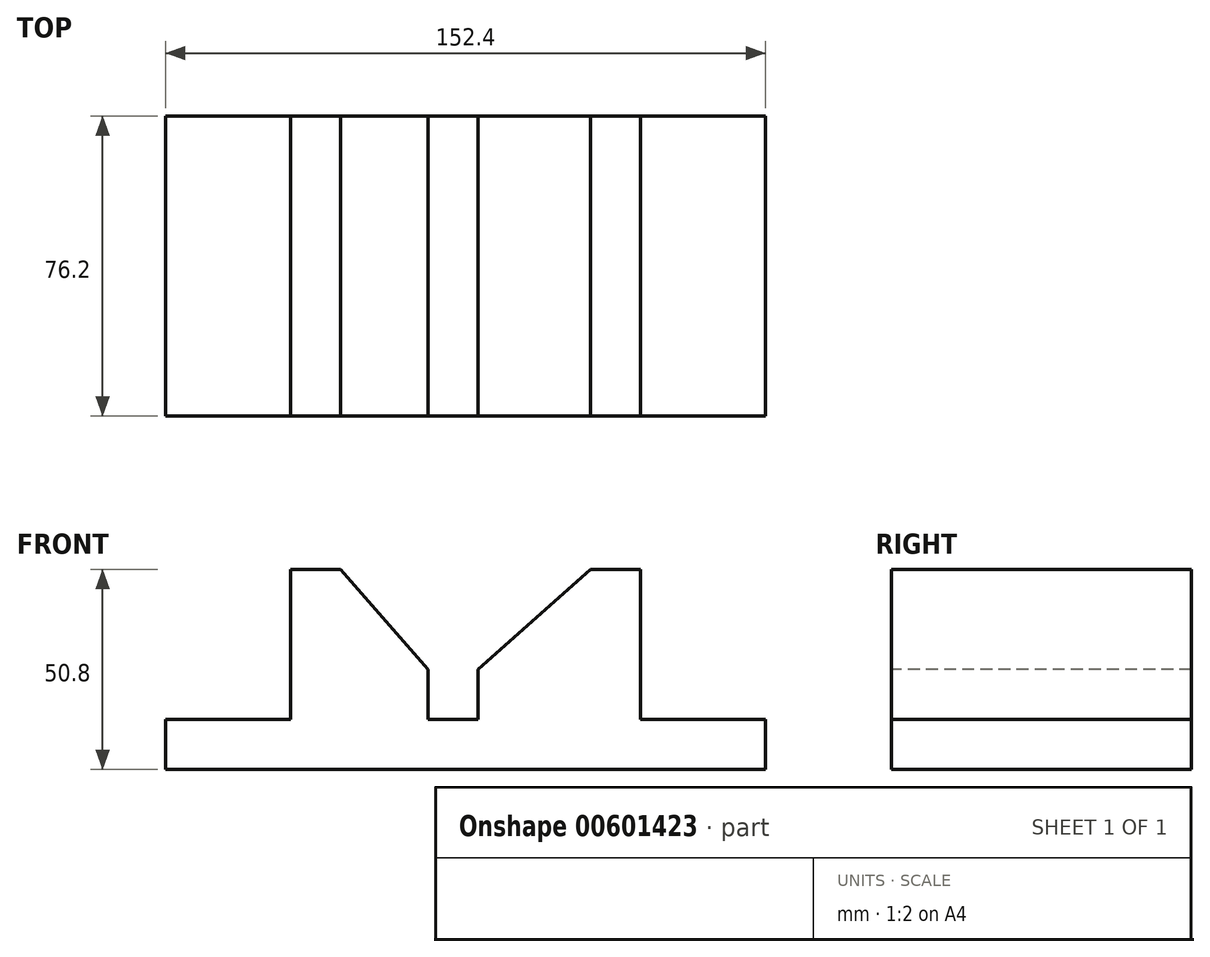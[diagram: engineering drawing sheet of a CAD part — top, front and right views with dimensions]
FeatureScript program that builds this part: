
annotation { "Feature Type Name" : "Feature", "Feature Type Description" : "" }
export const myFeature = defineFeature(function(context is Context, id is Id, definition is map)
    precondition{}
    {
        {
            var Q0;
            Q0=qCreatedBy(makeId("Front.planeOp"),FACE);
            var sketch = newSketch(context, id + "F0", { "sketchPlane" : qUnion([Q0])});
            skLineSegment(sketch, "E0", {"start": v(0, 0) * mm, "end": v(0, 12.7) * mm});
            skLineSegment(sketch, "E1", {"start": v(0, 12.7) * mm, "end": v(31.75, 12.7) * mm});
            skLineSegment(sketch, "E2", {"start": v(31.75, 12.7) * mm, "end": v(31.75, 50.8) * mm});
            skLineSegment(sketch, "E3", {"start": v(31.75, 50.8) * mm, "end": v(44.45, 50.8) * mm});
            skLineSegment(sketch, "E4", {"start": v(44.45, 50.8) * mm, "end": v(66.63, 25.4) * mm});
            skLineSegment(sketch, "E5", {"start": v(66.63, 25.4) * mm, "end": v(66.63, 12.7) * mm});
            skLineSegment(sketch, "E6", {"start": v(66.63, 12.7) * mm, "end": v(79.33, 12.7) * mm});
            skLineSegment(sketch, "E7", {"start": v(79.33, 12.7) * mm, "end": v(79.33, 25.4) * mm});
            skLineSegment(sketch, "E8", {"start": v(79.33, 25.4) * mm, "end": v(107.95, 50.8) * mm});
            skLineSegment(sketch, "E9", {"start": v(107.95, 50.8) * mm, "end": v(120.65, 50.8) * mm});
            skLineSegment(sketch, "E10", {"start": v(120.65, 50.8) * mm, "end": v(120.65, 12.7) * mm});
            skLineSegment(sketch, "E11", {"start": v(120.65, 12.7) * mm, "end": v(152.4, 12.7) * mm});
            skLineSegment(sketch, "E12", {"start": v(152.4, 12.7) * mm, "end": v(152.4, 0) * mm});
            skLineSegment(sketch, "E13", {"start": v(152.4, 0) * mm, "end": v(0, 0) * mm});
            skSolve(sketch);
        }
        {
            var Q0;
            Q0=makeQuery(id+"F0.imprint","IMPRINT",FACE,{"disambiguationData":[TD([[makeQuery(id+"F0.imprint","IMPRINT",EDGE,{"derivedFrom":sQuery(id+"F0.wireOp",EDGE,"E0")}),-1.0]])]});
            extrude(context, id + "F1", {"entities" : qUnion([Q0]), "oppositeDirection" : true, "depth" : 76.2 * mm, "offsetDistance" : 25.4 * mm});
        }
    });
